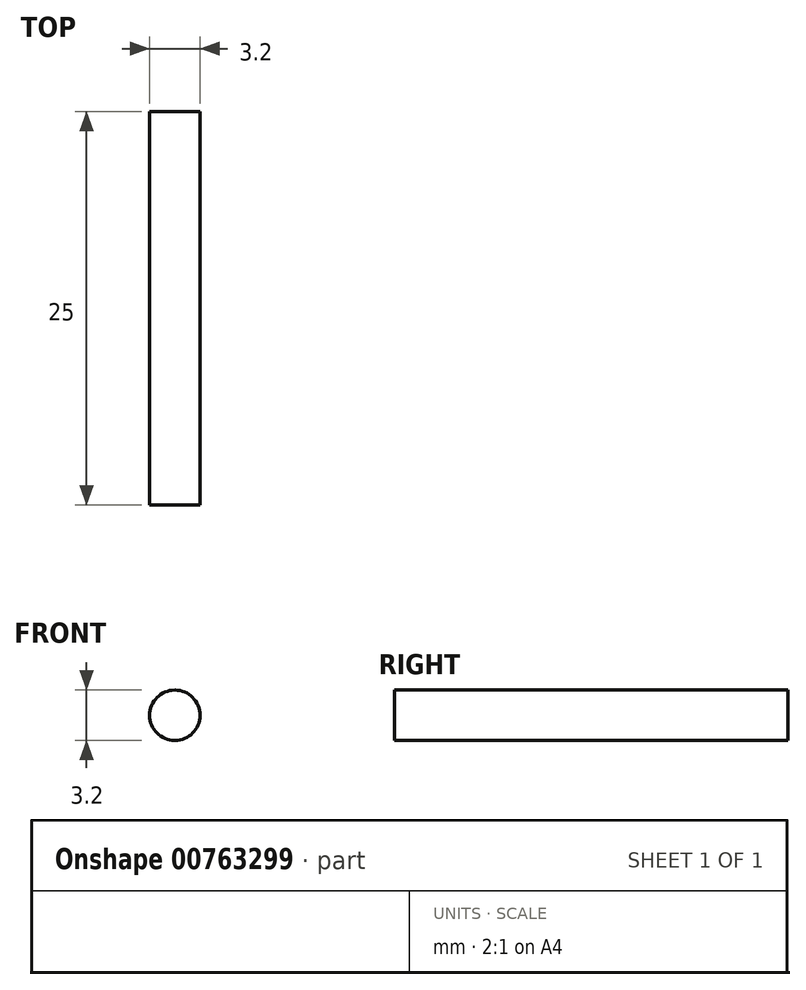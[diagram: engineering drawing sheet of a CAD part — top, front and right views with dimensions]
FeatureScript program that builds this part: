
annotation { "Feature Type Name" : "Feature", "Feature Type Description" : "" }
export const myFeature = defineFeature(function(context is Context, id is Id, definition is map)
    precondition{}
    {
        {
            var Q0;
            Q0=qCreatedBy(makeId("Front.planeOp"),FACE);
            var sketch = newSketch(context, id + "F0", { "sketchPlane" : qUnion([Q0])});
            skCircle(sketch, "E0", {"center": v(0, 0) * mm, "radius": 1.6 * mm});
            skSolve(sketch);
        }
        {
            var Q0;
            Q0=makeQuery(id+"F0.imprint","IMPRINT",FACE,{"disambiguationData":[TD([[makeQuery(id+"F0.imprint","IMPRINT",EDGE,{"derivedFrom":sQuery(id+"F0.wireOp",EDGE,"E0")}),1.0]])]});
            extrude(context, id + "F1", {"entities" : qUnion([Q0]), "oppositeDirection" : true, "depth" : 25 * mm, "offsetDistance" : 25 * mm});
        }
    });
